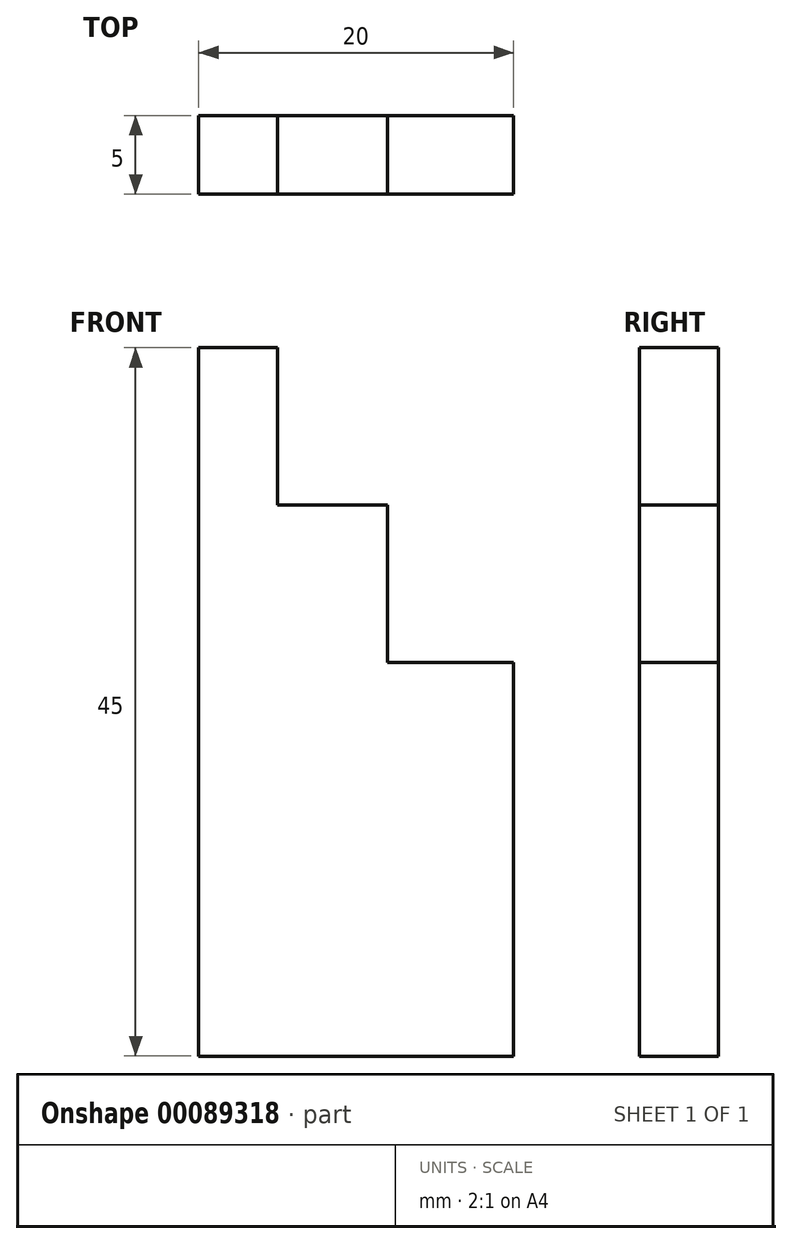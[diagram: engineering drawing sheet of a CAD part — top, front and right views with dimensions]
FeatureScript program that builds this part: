
annotation { "Feature Type Name" : "Feature", "Feature Type Description" : "" }
export const myFeature = defineFeature(function(context is Context, id is Id, definition is map)
    precondition{}
    {
        {
            var Q0;
            Q0=qCreatedBy(makeId("Front.planeOp"),FACE);
            var sketch = newSketch(context, id + "F0", { "sketchPlane" : qUnion([Q0])});
            skLineSegment(sketch, "E0", {"start": v(0, 27.92) * mm, "end": v(0, -17.08) * mm});
            skLineSegment(sketch, "E1", {"start": v(0, 27.92) * mm, "end": v(5, 27.92) * mm});
            skLineSegment(sketch, "E2", {"start": v(5, 27.92) * mm, "end": v(5, 17.92) * mm});
            skLineSegment(sketch, "E3", {"start": v(5, 17.92) * mm, "end": v(12, 17.92) * mm});
            skLineSegment(sketch, "E4", {"start": v(12, 17.92) * mm, "end": v(12, 7.92) * mm});
            skLineSegment(sketch, "E5", {"start": v(12, 7.92) * mm, "end": v(20, 7.92) * mm});
            skLineSegment(sketch, "E6", {"start": v(20, 7.92) * mm, "end": v(20, -17.08) * mm});
            skLineSegment(sketch, "E7", {"start": v(0, -17.08) * mm, "end": v(20, -17.08) * mm});
            skSolve(sketch);
        }
        {
            var Q0;
            Q0 = qSketchRegion(id + "F0", true);
            extrude(context, id + "F1", {"entities" : qUnion([Q0]), "depth" : 5 * mm});
        }
    });
